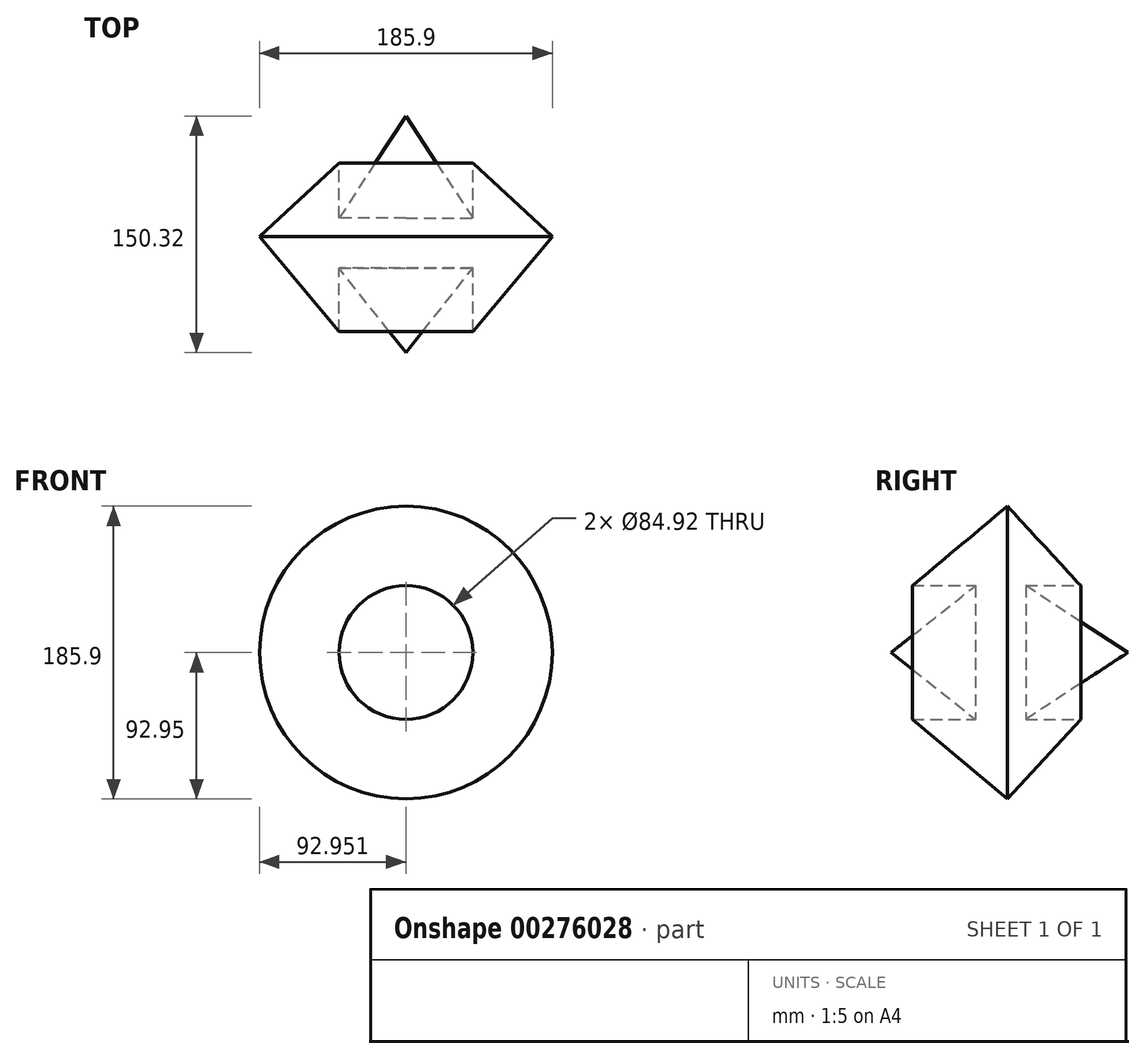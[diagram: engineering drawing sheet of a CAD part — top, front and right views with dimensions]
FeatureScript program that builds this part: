
annotation { "Feature Type Name" : "Feature", "Feature Type Description" : "" }
export const myFeature = defineFeature(function(context is Context, id is Id, definition is map)
    precondition{}
    {
        {
            var Q0;
            Q0=qCreatedBy(makeId("Top.planeOp"),FACE);
            var sketch = newSketch(context, id + "F0", { "sketchPlane" : qUnion([Q0])});
            skLineSegment(sketch, "E0", {"start": v(-42.46, 76.45) * mm, "end": v(-42.46, -73.87) * mm});
            skLineSegment(sketch, "E1", {"start": v(-42.46, -73.87) * mm, "end": v(0, -20.23) * mm});
            skLineSegment(sketch, "E2", {"start": v(0, -60.39) * mm, "end": v(0, -20.23) * mm});
            skLineSegment(sketch, "E3", {"start": v(0, -60.39) * mm, "end": v(50.5, 0) * mm});
            skLineSegment(sketch, "E4", {"start": v(50.5, 0) * mm, "end": v(0, 46.62) * mm});
            skLineSegment(sketch, "E5", {"start": v(0, 46.62) * mm, "end": v(0, 10.76) * mm});
            skLineSegment(sketch, "E6", {"start": v(0.57, 10.76) * mm, "end": v(-42.46, 76.45) * mm});
            skSolve(sketch);
        }
        {
            var Q0;
            {var subQ0=sQuery(id+"F0.wireOp",EDGE,"E0");Q0=makeQuery(id+"F0.imprint","IMPRINT",FACE,{"disambiguationData":[TD([[makeQuery(id+"F0.imprint","IMPRINT",EDGE,{"derivedFrom":subQ0}),1.0]])]});}
            var Q1;
            Q1=sQuery(id+"F0.wireOp",EDGE,"E0");
            revolve(context, id + "F1", {"entities" : qUnion([Q0]), "axis" : qUnion([Q1]), "revolveType" : RevolveType.FULL});
        }
    });
